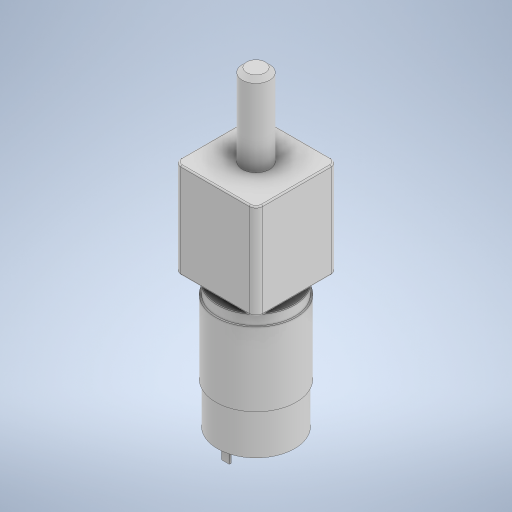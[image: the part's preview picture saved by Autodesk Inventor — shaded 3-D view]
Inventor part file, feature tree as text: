
AUTODESK INVENTOR PART (.ipt)
format: ipt  version: 2024 (Build 280153000, 153)  size: 374,272 bytes
history: native  units: in
note: dims shown in document units (in); Inventor stores cm internally (conversion verified against a paired STEP export)
features: extrude x10, fillet x6, sketch x4, chamfer x1
ambient origin geometry x8: Origin, YZ Plane, XZ Plane, XY Plane, X Axis, Y Axis, Z Axis, Center Point
bodies: Solid1 (feature_tree)
feature tree (21):
  extrude  "Extrusion1"  Depth=0.755in TaperAngle=0.0deg
  extrude  "Extrusion2"  Depth=1.35in TaperAngle=0.0deg
  extrude  "Extrusion3"  Depth=0.19in TaperAngle=0.0deg
  extrude  "Extrusion4"  Depth=0.17in TaperAngle=0.0deg
  extrude  "Extrusion5"  Depth=0.125in
  fillet  "Fillet1"  Radius=0.326in
  fillet  "Fillet2"  Radius=0.0125in
  extrude  "Extrusion6"  Depth=0.0125in
  extrude  "Extrusion7"  Depth=0.125in
  fillet  "Fillet3"  Radius=0.144in
  extrude  "Extrusion8"  Depth=0.073in TaperAngle=0.0deg
  fillet  "Fillet4"  Radius=0.025in
  extrude  "Extrusion9"  Depth=0.125in
  fillet  "Fillet5"  Radius=0.025in
  fillet  "Fillet6"  Radius=0.025in
  extrude  "Extrusion10"  Depth=0.125in
  chamfer  "Chamfer1"  Distance=0.151in
  sketch  "Sketch7"  dims[d0=1.415in d1=0.755in d2=0.0in]
  sketch  "Sketch8"  dims[d3=1.475in d4=1.35in d5=0.0in]
  sketch  "Sketch9"  dims[d6=1.415in d7=0.19in d8=0.0in]
  sketch  "Sketch10"  dims[d9=0.51in d10=0.17in d11=0.0in d12=0.125in d13=0.326in d14=0.0in d15=0.0125in d16=0.0125in d17=0.512in d18=0.144in d19=0.0in d20=0.073in d21=0.0in d22=0.025in d24=0.532in d26=0.025in d27=0.025in d28=0.532in d29=0.151in d30=0.151in d31=0.0in d32=0.29in d33=0.0in d34=0.0125in d35=1.505in d36=1.505in d37=1.75in d38=0.0in d39=0.125in d40=0.025in d41=0.5in d42=1.5in d43=0.0in d44=0.08in d45=0.125in d46=45.0deg]
